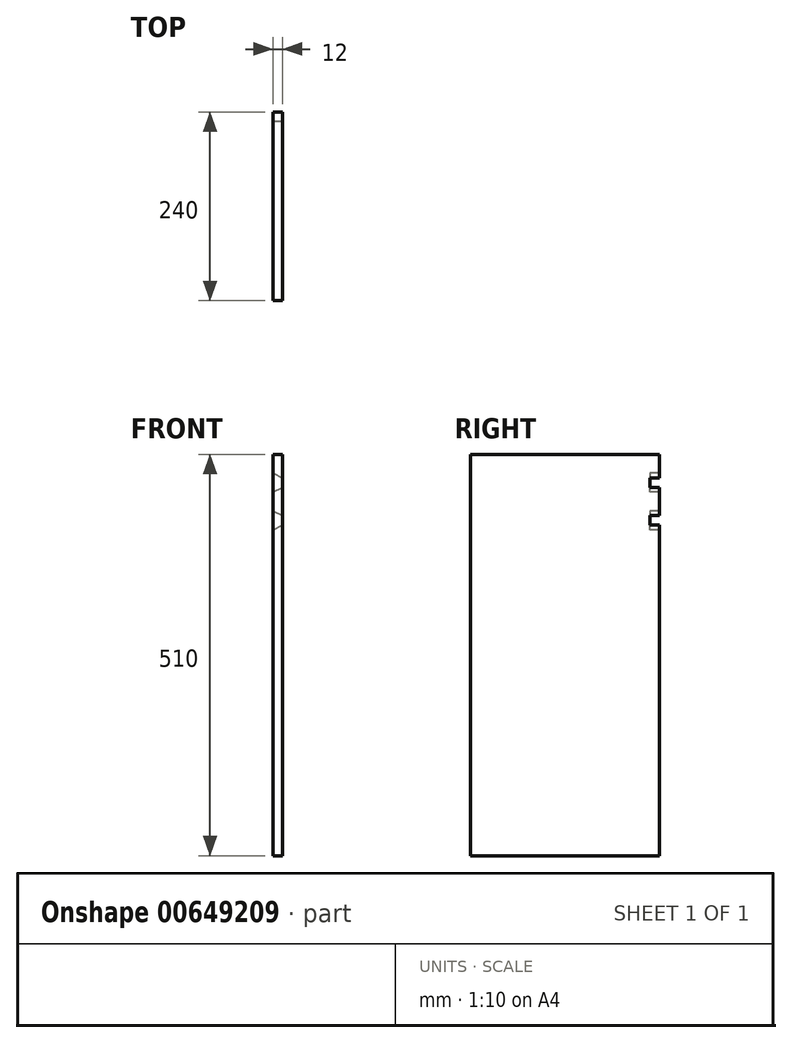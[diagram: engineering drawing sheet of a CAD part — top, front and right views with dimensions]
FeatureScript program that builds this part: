
annotation { "Feature Type Name" : "Feature", "Feature Type Description" : "" }
export const myFeature = defineFeature(function(context is Context, id is Id, definition is map)
    precondition{}
    {
        {
            var Q0;
            Q0=qCreatedBy(makeId("Right.planeOp"),FACE);
            var sketch = newSketch(context, id + "F0", { "sketchPlane" : qUnion([Q0])});
            skLineSegment(sketch, "E0.bottom", {"start": v(120, 261) * mm, "end": v(-120, 261) * mm});
            skLineSegment(sketch, "E0.top", {"start": v(120, -261) * mm, "end": v(-120, -261) * mm});
            skLineSegment(sketch, "E0.left", {"start": v(120, 261) * mm, "end": v(120, -261) * mm});
            skLineSegment(sketch, "E0.right", {"start": v(-120, 261) * mm, "end": v(-120, -261) * mm});
            skPoint(sketch, "E0.middle", {"position": v(0, 0) * mm});
            skLineSegment(sketch, "E1", {"start": v(108, 261) * mm, "end": v(108, -261) * mm, "construction": true});
            skLineSegment(sketch, "E2", {"start": v(108, 254.77) * mm, "end": v(120, 254.77) * mm, "construction": true});
            skLineSegment(sketch, "E3", {"start": v(120, 249) * mm, "end": v(-120, 249) * mm, "construction": true});
            skLineSegment(sketch, "E4", {"start": v(-118, 261) * mm, "end": v(-118, 249) * mm, "construction": true});
            skLineSegment(sketch, "E5.bottom", {"start": v(-96, 261) * mm, "end": v(-72, 261) * mm});
            skLineSegment(sketch, "E5.top", {"start": v(-96, 249) * mm, "end": v(-72, 249) * mm});
            skLineSegment(sketch, "E5.left", {"start": v(-96, 261) * mm, "end": v(-96, 249) * mm});
            skLineSegment(sketch, "E5.right", {"start": v(-72, 261) * mm, "end": v(-72, 249) * mm});
            skLineSegment(sketch, "E6.bottom", {"start": v(-48, 261) * mm, "end": v(-24, 261) * mm});
            skLineSegment(sketch, "E6.top", {"start": v(-48, 249) * mm, "end": v(-24, 249) * mm});
            skLineSegment(sketch, "E6.left", {"start": v(-48, 261) * mm, "end": v(-48, 249) * mm});
            skLineSegment(sketch, "E6.right", {"start": v(-24, 261) * mm, "end": v(-24, 249) * mm});
            skLineSegment(sketch, "E7.bottom", {"start": v(24, 261) * mm, "end": v(48, 261) * mm});
            skLineSegment(sketch, "E7.top", {"start": v(24, 249) * mm, "end": v(48, 249) * mm});
            skLineSegment(sketch, "E7.left", {"start": v(24, 261) * mm, "end": v(24, 249) * mm});
            skLineSegment(sketch, "E7.right", {"start": v(48, 261) * mm, "end": v(48, 249) * mm});
            skLineSegment(sketch, "E8.bottom", {"start": v(72, 261) * mm, "end": v(96, 261) * mm});
            skLineSegment(sketch, "E8.top", {"start": v(72, 249) * mm, "end": v(96, 249) * mm});
            skLineSegment(sketch, "E8.left", {"start": v(72, 261) * mm, "end": v(72, 249) * mm});
            skLineSegment(sketch, "E8.right", {"start": v(96, 261) * mm, "end": v(96, 249) * mm});
            skLineSegment(sketch, "E9", {"start": v(120, 252.12) * mm, "end": v(96, 252.12) * mm, "construction": true});
            skLineSegment(sketch, "E10", {"start": v(72, 255) * mm, "end": v(48, 255) * mm, "construction": true});
            skLineSegment(sketch, "E11", {"start": v(-48, 255) * mm, "end": v(-72, 255) * mm, "construction": true});
            skLineSegment(sketch, "E12", {"start": v(-96, 255) * mm, "end": v(-120, 255) * mm, "construction": true});
            skLineSegment(sketch, "E13", {"start": v(-96, 261) * mm, "end": v(-90, 249) * mm});
            skLineSegment(sketch, "E14", {"start": v(-90, 249) * mm, "end": v(-96, 249) * mm});
            skLineSegment(sketch, "E15", {"start": v(-72, 261) * mm, "end": v(-78, 249) * mm});
            skLineSegment(sketch, "E16", {"start": v(-78, 249) * mm, "end": v(-72, 249) * mm});
            skLineSegment(sketch, "E17", {"start": v(-48, 261) * mm, "end": v(-42, 249) * mm});
            skLineSegment(sketch, "E18", {"start": v(-42, 249) * mm, "end": v(-48, 249) * mm});
            skLineSegment(sketch, "E19", {"start": v(-24, 249) * mm, "end": v(-30, 249) * mm});
            skLineSegment(sketch, "E20", {"start": v(-30, 249) * mm, "end": v(-24, 261) * mm});
            skLineSegment(sketch, "E21", {"start": v(96, 261) * mm, "end": v(90, 249) * mm});
            skLineSegment(sketch, "E22", {"start": v(90, 249) * mm, "end": v(96, 249) * mm});
            skLineSegment(sketch, "E23", {"start": v(78, 249) * mm, "end": v(72, 249) * mm});
            skLineSegment(sketch, "E24", {"start": v(78, 249) * mm, "end": v(72, 261) * mm});
            skLineSegment(sketch, "E25", {"start": v(48, 261) * mm, "end": v(42, 249) * mm});
            skLineSegment(sketch, "E26", {"start": v(42, 249) * mm, "end": v(48, 249) * mm});
            skLineSegment(sketch, "E27", {"start": v(24, 249) * mm, "end": v(30, 249) * mm});
            skLineSegment(sketch, "E28", {"start": v(30, 249) * mm, "end": v(24, 261) * mm});
            skLineSegment(sketch, "E29", {"start": v(96, 249) * mm, "end": v(120, 249) * mm});
            skLineSegment(sketch, "E30", {"start": v(72, 249) * mm, "end": v(48, 249) * mm});
            skLineSegment(sketch, "E31", {"start": v(24, 249) * mm, "end": v(-24, 249) * mm});
            skLineSegment(sketch, "E32", {"start": v(-48, 249) * mm, "end": v(-72, 249) * mm});
            skLineSegment(sketch, "E33", {"start": v(-96, 249) * mm, "end": v(-120, 249) * mm});
            skLineSegment(sketch, "E34", {"start": v(114, 249) * mm, "end": v(114, 225) * mm, "construction": true});
            skLineSegment(sketch, "E35.bottom", {"start": v(120, 225) * mm, "end": v(108, 225) * mm});
            skLineSegment(sketch, "E35.top", {"start": v(120, 201) * mm, "end": v(108, 201) * mm});
            skLineSegment(sketch, "E35.left", {"start": v(120, 225) * mm, "end": v(120, 201) * mm});
            skLineSegment(sketch, "E35.right", {"start": v(108, 225) * mm, "end": v(108, 201) * mm});
            skPoint(sketch, "E36", {"position": v(114, 225) * mm});
            skLineSegment(sketch, "E37.bottom", {"start": v(120, 177) * mm, "end": v(108, 177) * mm});
            skLineSegment(sketch, "E37.top", {"start": v(120, 153) * mm, "end": v(108, 153) * mm});
            skLineSegment(sketch, "E37.left", {"start": v(120, 177) * mm, "end": v(120, 153) * mm});
            skLineSegment(sketch, "E37.right", {"start": v(108, 177) * mm, "end": v(108, 153) * mm});
            skLineSegment(sketch, "E38", {"start": v(114, 201) * mm, "end": v(114, 177) * mm, "construction": true});
            skSolve(sketch);
        }
        {
            var Q0;
            {var subQ0=sQuery(id+"F0.wireOp",EDGE,"E0.top");Q0=makeQuery(id+"F0.imprint","IMPRINT",FACE,{"disambiguationData":[TD([[makeQuery(id+"F0.imprint","IMPRINT",EDGE,{"derivedFrom":subQ0}),-1.0]])]});}
            var Q1;
            Q1=makeQuery(id+"F0.imprint","IMPRINT",FACE,{"disambiguationData":[TD([[makeQuery(id+"F0.imprint","IMPRINT",EDGE,{"derivedFrom":sQuery(id+"F0.wireOp",EDGE,"E5.bottom")}),-1.0]])]});
            var Q2;
            Q2=makeQuery(id+"F0.imprint","IMPRINT",FACE,{"disambiguationData":[TD([[makeQuery(id+"F0.imprint","IMPRINT",EDGE,{"derivedFrom":sQuery(id+"F0.wireOp",EDGE,"E6.bottom")}),-1.0]])]});
            var Q3;
            Q3=makeQuery(id+"F0.imprint","IMPRINT",FACE,{"disambiguationData":[TD([[makeQuery(id+"F0.imprint","IMPRINT",EDGE,{"derivedFrom":sQuery(id+"F0.wireOp",EDGE,"E7.bottom")}),-1.0]])]});
            var Q4;
            Q4=makeQuery(id+"F0.imprint","IMPRINT",FACE,{"disambiguationData":[TD([[makeQuery(id+"F0.imprint","IMPRINT",EDGE,{"derivedFrom":sQuery(id+"F0.wireOp",EDGE,"E8.bottom")}),-1.0]])]});
            extrude(context, id + "F1", {"entities" : qUnion([Q0, Q1, Q2, Q3, Q4]), "depth" : 12 * mm, "offsetDistance" : 25 * mm});
        }
        {
            var Q0;
            Q0=makeQuery(id+"F1.opExtrude","SWEPT_FACE",FACE,{"disambiguationData":[OSD([sQuery(id+"F0.wireOp",EDGE,"E35.right")])]});
            var sketch = newSketch(context, id + "F2", { "sketchPlane" : qUnion([Q0])});
            skLineSegment(sketch, "E39", {"start": v(0, 225) * mm, "end": v(-12, 219) * mm});
            skLineSegment(sketch, "E40", {"start": v(-12, 219) * mm, "end": v(-12, 225) * mm});
            skLineSegment(sketch, "E41", {"start": v(-12, 225) * mm, "end": v(0, 225) * mm});
            skLineSegment(sketch, "E42", {"start": v(0, 201) * mm, "end": v(-12, 207) * mm});
            skLineSegment(sketch, "E43", {"start": v(-12, 207) * mm, "end": v(-12, 201) * mm});
            skLineSegment(sketch, "E44", {"start": v(-12, 201) * mm, "end": v(0, 201) * mm});
            skSolve(sketch);
        }
        {
            var Q0;
            Q0 = qSketchRegion(id + "F2", true);
            extrude(context, id + "F3", {"entities" : qUnion([Q0]), "operationType" : NewBodyOperationType.ADD, "depth" : 12 * mm, "offsetDistance" : 25 * mm});
        }
        {
            var Q0;
            Q0=makeQuery(id+"F1.opExtrude","SWEPT_FACE",FACE,{"disambiguationData":[OSD([sQuery(id+"F0.wireOp",EDGE,"E37.right")])]});
            var sketch = newSketch(context, id + "F4", { "sketchPlane" : qUnion([Q0])});
            skLineSegment(sketch, "E45", {"start": v(0, 177) * mm, "end": v(-12, 171) * mm});
            skLineSegment(sketch, "E46", {"start": v(-12, 171) * mm, "end": v(-12, 177) * mm});
            skLineSegment(sketch, "E47", {"start": v(-12, 177) * mm, "end": v(0, 177) * mm});
            skLineSegment(sketch, "E48", {"start": v(0, 153) * mm, "end": v(-12, 159) * mm});
            skLineSegment(sketch, "E49", {"start": v(-12, 159) * mm, "end": v(-12, 153) * mm});
            skLineSegment(sketch, "E50", {"start": v(-12, 153) * mm, "end": v(0, 153) * mm});
            skSolve(sketch);
        }
        {
            var Q0;
            Q0 = qSketchRegion(id + "F4", true);
            extrude(context, id + "F5", {"entities" : qUnion([Q0]), "operationType" : NewBodyOperationType.ADD, "depth" : 12 * mm, "offsetDistance" : 25 * mm});
        }
    });
